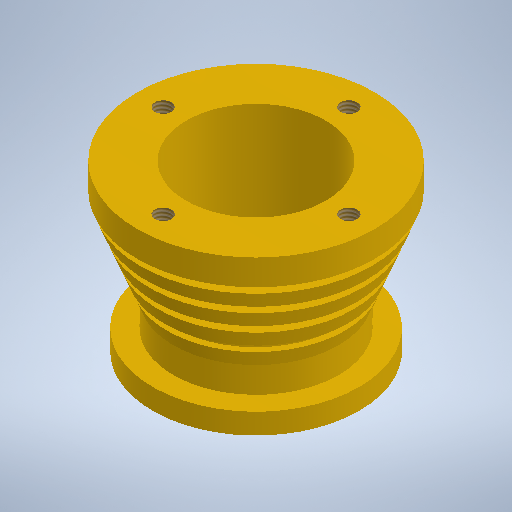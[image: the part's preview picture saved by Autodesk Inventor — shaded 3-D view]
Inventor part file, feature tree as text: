
AUTODESK INVENTOR PART (.ipt)
format: ipt  version: 2025 (Build 290162010, 162A)  size: 326,656 bytes
history: native  units: mm
features: sketch x3, hole x2, revolve x1
ambient origin geometry x8: Origin, YZ Plane, XZ Plane, XY Plane, X Axis, Y Axis, Z Axis, Center Point
bodies: Volumenkörper1 (feature_tree)
feature tree (6):
  revolve  "Umdrehung1"
  hole  "Bohrung1"  [1 undecoded]
  hole  "Bohrung2"  [1 undecoded]
  sketch  "Skizze1"  dims[d18=32.0mm d21=4.0mm]
  sketch  "Skizze2"  dims[d26=46.0mm d27=40.0mm]
  sketch  "Skizze3"  dims[d28=32.0mm d29=18.0mm d30=5.0mm d34=5.0mm d35=1.5mm d36=1.5mm d37=1.5mm d38=1.5mm d42=3.0mm d43=3.0mm d44=3.0mm d45=90.0deg d46=36.0mm d47=3.242mm d48=8.0mm d49=4.0mm d50=2.0mm d51=90.0deg d52=8.0mm d53=0.0mm d54=27.0mm d55=8.0mm d56=4.0mm d57=2.0mm d58=90.0deg d59=8.0mm d60=0.0mm]
note: 2 required parameter values undecoded (feature->parameter linkage not recoverable at this tier; creation-order binding heuristic only, values carry confidence <= 0.55)
